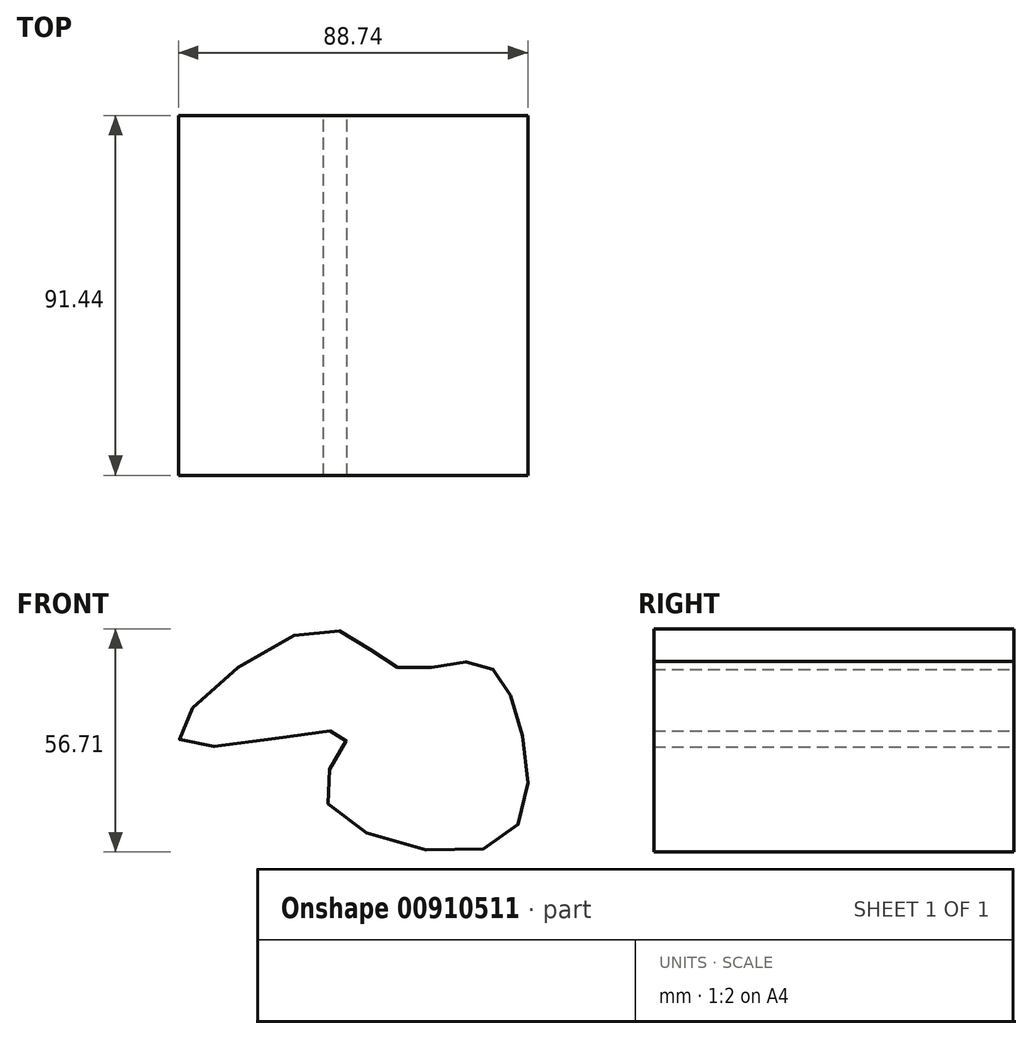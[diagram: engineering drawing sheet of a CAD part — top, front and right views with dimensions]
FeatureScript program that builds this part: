
annotation { "Feature Type Name" : "Feature", "Feature Type Description" : "" }
export const myFeature = defineFeature(function(context is Context, id is Id, definition is map)
    precondition{}
    {
        {
            var Q0;
            Q0=qCreatedBy(makeId("Front.planeOp"),FACE);
            var sketch = newSketch(context, id + "F0", { "sketchPlane" : qUnion([Q0])});
            skFitSpline(sketch, "E0", {"points": [v(-57.42, 56.15) * mm, v(-36.9, 57.4) * mm, v(-26.46, 41.69) * mm, v(-32.22, 11.22) * mm, v(-76.15, 24.1) * mm, v(-70.75, 39.34) * mm, v(-112.5, 37.37) * mm, v(-77.59, 65.81) * mm, v(-57.42, 56.15) * mm]});
            skSolve(sketch);
        }
        {
            var Q0;
            Q0=makeQuery(id+"F0.imprint","IMPRINT",FACE,{"disambiguationData":[TD([[makeQuery(id+"F0.imprint","IMPRINT",EDGE,{"derivedFrom":sQuery(id+"F0.wireOp",EDGE,"E0")}),-1.0]])]});
            extrude(context, id + "F1", {"entities" : qUnion([Q0]), "depth" : 91.44 * mm, "offsetDistance" : 25.4 * mm});
        }
    });
